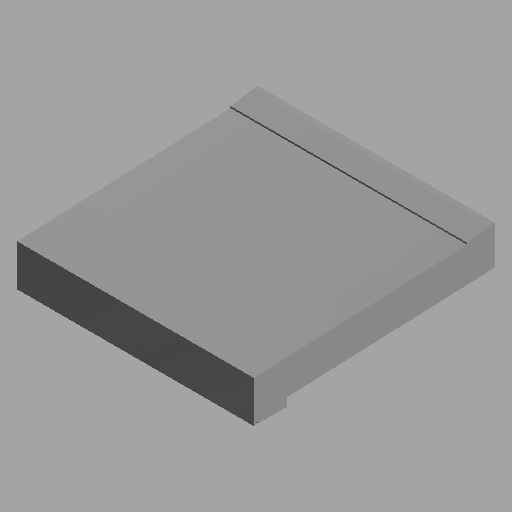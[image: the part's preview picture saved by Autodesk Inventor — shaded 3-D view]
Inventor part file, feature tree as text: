
AUTODESK INVENTOR PART (.ipt)
format: ipt  version: 2023 (Build 270158000, 158)  size: 100,864 bytes
history: native  units: mm (DEFAULTED — no unit token found)
features: extrude x1, sketch x1
ambient origin geometry x8: Origin, YZ Plane, XZ Plane, XY Plane, X Axis, Y Axis, Z Axis, Center Point
bodies: Solid1 (feature_tree), Body1 (feature_tree)
feature tree (2):
  extrude  "Extrusion1"  [1 undecoded]
  sketch  "Sketch2"  dims[d0=0.0mm d1=0.0mm]
note: 1 required parameter value undecoded (feature->parameter linkage not recoverable at this tier; creation-order binding heuristic only, values carry confidence <= 0.55)
